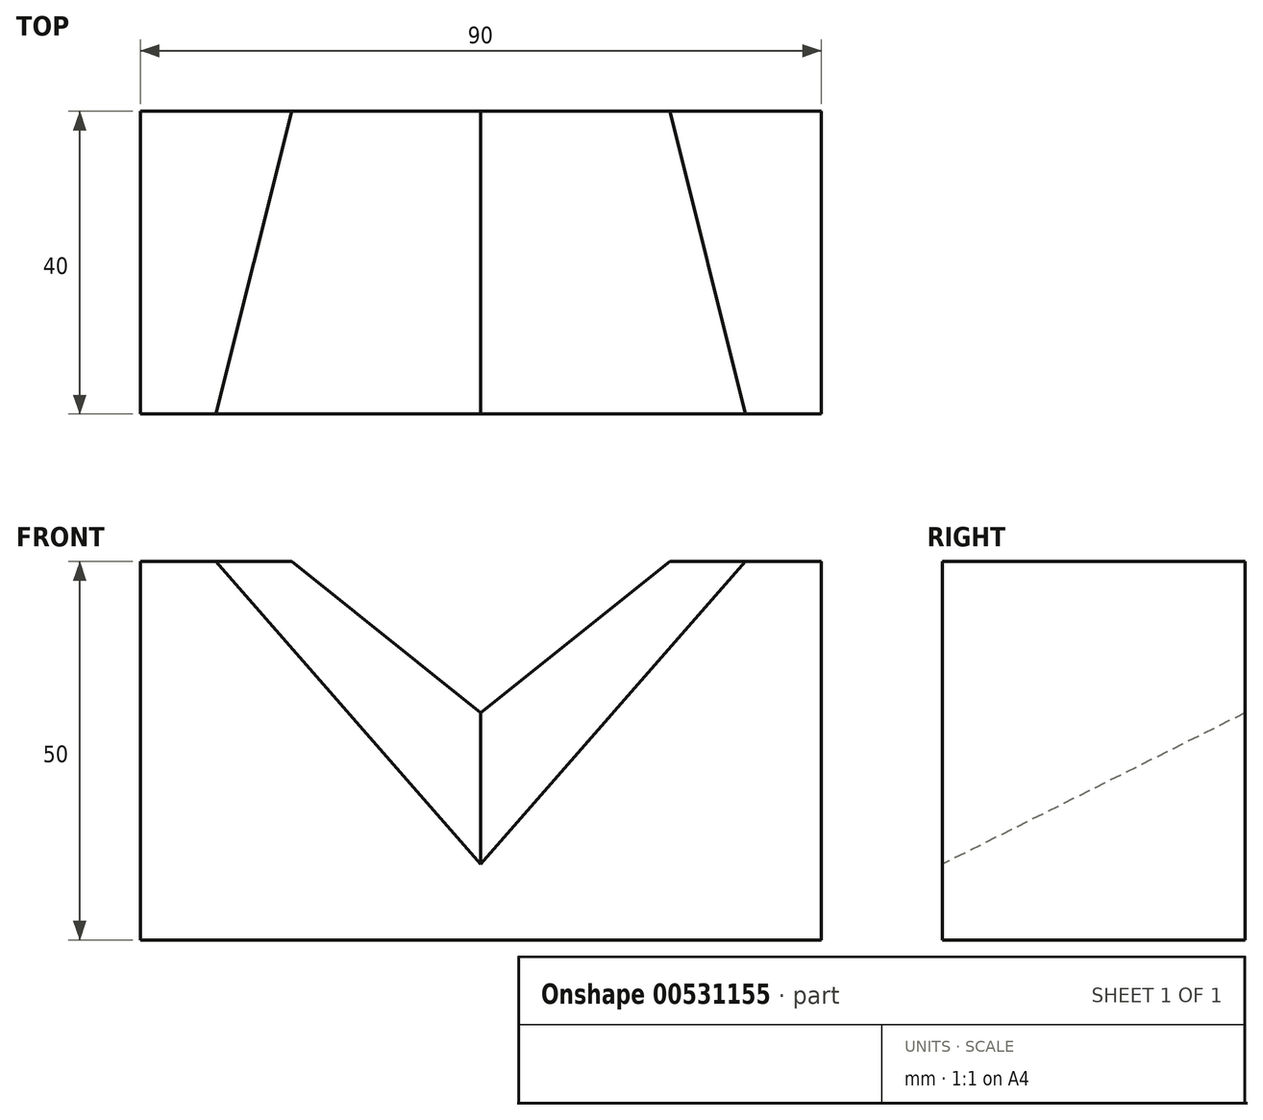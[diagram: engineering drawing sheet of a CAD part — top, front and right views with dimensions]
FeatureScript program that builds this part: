
annotation { "Feature Type Name" : "Feature", "Feature Type Description" : "" }
export const myFeature = defineFeature(function(context is Context, id is Id, definition is map)
    precondition{}
    {
        {
            var Q0;
            Q0=qCreatedBy(makeId("Top.planeOp"),FACE);
            var sketch = newSketch(context, id + "F0", { "sketchPlane" : qUnion([Q0])});
            skLineSegment(sketch, "E0.bottom", {"start": v(0, 0) * mm, "end": v(90, 0) * mm});
            skLineSegment(sketch, "E0.top", {"start": v(0, 40) * mm, "end": v(90, 40) * mm});
            skLineSegment(sketch, "E0.left", {"start": v(0, 0) * mm, "end": v(0, 40) * mm});
            skLineSegment(sketch, "E0.right", {"start": v(90, 0) * mm, "end": v(90, 40) * mm});
            skSolve(sketch);
        }
        {
            var Q0;
            Q0 = qSketchRegion(id + "F0", true);
            extrude(context, id + "F1", {"entities" : qUnion([Q0]), "depth" : 50 * mm, "offsetDistance" : 25.4 * mm});
        }
        {
            var Q0;
            Q0=makeQuery(id+"F1.opExtrude","SWEPT_FACE",FACE,{"disambiguationData":[OSD([sQuery(id+"F0.wireOp",EDGE,"E0.bottom")])]});
            var sketch = newSketch(context, id + "F2", { "sketchPlane" : qUnion([Q0])});
            skLineSegment(sketch, "E1", {"start": v(0, 50) * mm, "end": v(10, 50) * mm, "construction": true});
            skLineSegment(sketch, "E2", {"start": v(90, 50) * mm, "end": v(80, 50) * mm, "construction": true});
            skLineSegment(sketch, "E3", {"start": v(45, 0) * mm, "end": v(45, 10) * mm, "construction": true});
            skLineSegment(sketch, "E4", {"start": v(10, 50) * mm, "end": v(45, 10) * mm});
            skLineSegment(sketch, "E5", {"start": v(80, 50) * mm, "end": v(45, 10) * mm});
            skLineSegment(sketch, "E6", {"start": v(80, 50) * mm, "end": v(10, 50) * mm});
            skSolve(sketch);
        }
        {
            var Q0;
            Q0=makeQuery(id+"F1.opExtrude","SWEPT_FACE",FACE,{"disambiguationData":[OSD([sQuery(id+"F0.wireOp",EDGE,"E0.top")])]});
            var sketch = newSketch(context, id + "F3", { "sketchPlane" : qUnion([Q0])});
            skLineSegment(sketch, "E7", {"start": v(-45, 0) * mm, "end": v(-45, 30) * mm, "construction": true});
            skLineSegment(sketch, "E8", {"start": v(-90, 50) * mm, "end": v(-70, 50) * mm, "construction": true});
            skLineSegment(sketch, "E9", {"start": v(0, 50) * mm, "end": v(-20, 50) * mm, "construction": true});
            skLineSegment(sketch, "E10", {"start": v(-20, 50) * mm, "end": v(-45, 30) * mm});
            skLineSegment(sketch, "E11", {"start": v(-70, 50) * mm, "end": v(-45, 30) * mm});
            skLineSegment(sketch, "E12", {"start": v(-70, 50) * mm, "end": v(-20, 50) * mm});
            skSolve(sketch);
        }
        {
            var Q1;
            Q1=makeQuery(id+"F3.imprint","IMPRINT",FACE,{"disambiguationData":[TD([[makeQuery(id+"F3.imprint","IMPRINT",EDGE,{"derivedFrom":sQuery(id+"F3.wireOp",EDGE,"E10")}),-1.0]])]});
            var Q2;
            Q2=makeQuery(id+"F2.imprint","IMPRINT",FACE,{"disambiguationData":[TD([[makeQuery(id+"F2.imprint","IMPRINT",EDGE,{"derivedFrom":sQuery(id+"F2.wireOp",EDGE,"E4")}),1.0]])]});
            loft(context, id + "F4", {"operationType" : NewBodyOperationType.REMOVE, "sheetProfilesArray" : [{ "sheetProfileEntities" : qUnion([Q1]) }, { "sheetProfileEntities" : qUnion([Q2]) }]});
        }
    });
